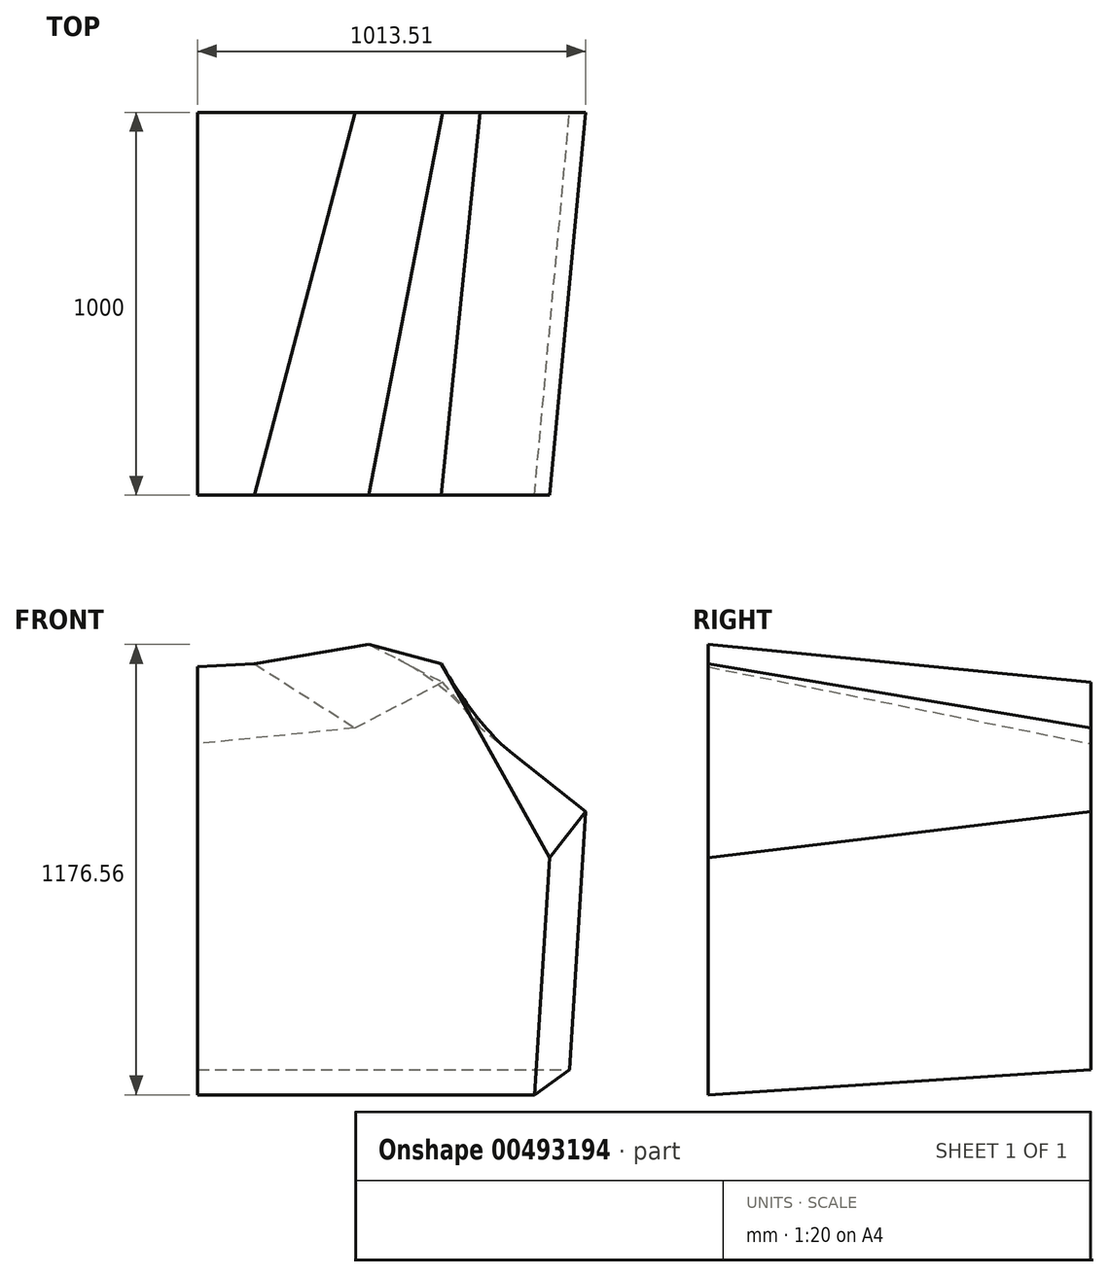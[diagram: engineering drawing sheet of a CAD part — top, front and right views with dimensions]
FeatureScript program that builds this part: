
annotation { "Feature Type Name" : "Feature", "Feature Type Description" : "" }
export const myFeature = defineFeature(function(context is Context, id is Id, definition is map)
    precondition{}
    {
        {
            var Q0;
            Q0=qCreatedBy(makeId("Front.planeOp"),FACE);
            var sketch = newSketch(context, id + "F0", { "sketchPlane" : qUnion([Q0])});
            skLineSegment(sketch, "E0", {"start": v(0, 0) * mm, "end": v(0, 850.8) * mm});
            skLineSegment(sketch, "E1", {"start": v(0, 0) * mm, "end": v(971.51, 0) * mm});
            skLineSegment(sketch, "E2", {"start": v(971.51, 0) * mm, "end": v(1004.74, 533.03) * mm});
            skLineSegment(sketch, "E3", {"start": v(1004.74, 533.03) * mm, "end": v(971.51, 0) * mm});
            skLineSegment(sketch, "E4", {"start": v(971.51, 0) * mm, "end": v(1013.5, 673.7) * mm});
            skLineSegment(sketch, "E5", {"start": v(1013.5, 673.7) * mm, "end": v(737.82, 892.07) * mm});
            skLineSegment(sketch, "E6", {"start": v(737.82, 892.07) * mm, "end": v(640.53, 1011.26) * mm});
            skLineSegment(sketch, "E7", {"start": v(640.53, 1011.26) * mm, "end": v(411.88, 892.07) * mm});
            skLineSegment(sketch, "E8", {"start": v(411.88, 892.07) * mm, "end": v(0, 850.8) * mm});
            skLineSegment(sketch, "E9", {"start": v(0, 850.8) * mm, "end": v(0, 850.8) * mm});
            skSolve(sketch);
        }
        {
            var Q0;
            Q0=makeQuery(id+"F0.imprint","IMPRINT",FACE,{"disambiguationData":[TD([[makeQuery(id+"F0.imprint","IMPRINT",EDGE,{"derivedFrom":sQuery(id+"F0.wireOp",EDGE,"E0")}),-1.0]])]});
            cPlane(context, id + "F1", {"entities" : qUnion([Q0]), "cplaneType" : CPlaneType.OFFSET, "offset" : 1000 * mm, "width" : 152.4 * mm, "height" : 152.4 * mm});
        }
        {
            var Q0;
            Q0=qCreatedBy(id+"F1.planeOp",FACE);
            var sketch = newSketch(context, id + "F2", { "sketchPlane" : qUnion([Q0])});
            skLineSegment(sketch, "E10", {"start": v(0, -66.19) * mm, "end": v(0, 1051.66) * mm});
            skLineSegment(sketch, "E11", {"start": v(0, -66.19) * mm, "end": v(879.93, -66.19) * mm});
            skLineSegment(sketch, "E12", {"start": v(879.93, -66.19) * mm, "end": v(913.65, 466.81) * mm});
            skLineSegment(sketch, "E13", {"start": v(913.65, 466.81) * mm, "end": v(879.93, -66.19) * mm});
            skLineSegment(sketch, "E14", {"start": v(879.93, -66.19) * mm, "end": v(919.13, 553.43) * mm});
            skLineSegment(sketch, "E15", {"start": v(919.13, 553.43) * mm, "end": v(636.53, 1059.64) * mm});
            skLineSegment(sketch, "E16", {"start": v(447.44, 1110.37) * mm, "end": v(636.53, 1059.64) * mm});
            skLineSegment(sketch, "E17", {"start": v(447.44, 1110.37) * mm, "end": v(148.94, 1059.64) * mm});
            skLineSegment(sketch, "E18", {"start": v(0, 1051.66) * mm, "end": v(148.94, 1059.64) * mm});
            skLineSegment(sketch, "E19", {"start": v(0, 1051.66) * mm, "end": v(0, 1051.66) * mm});
            skSolve(sketch);
        }
        {
            var Q0;
            Q0=makeQuery(id+"F2.imprint","IMPRINT",FACE,{"disambiguationData":[TD([[makeQuery(id+"F2.imprint","IMPRINT",EDGE,{"derivedFrom":sQuery(id+"F2.wireOp",EDGE,"E10")}),-1.0]])]});
            var Q1;
            Q1=makeQuery(id+"F0.imprint","IMPRINT",FACE,{"disambiguationData":[TD([[makeQuery(id+"F0.imprint","IMPRINT",EDGE,{"derivedFrom":sQuery(id+"F0.wireOp",EDGE,"E0")}),-1.0]])]});
            loft(context, id + "F3", {"sheetProfilesArray" : [{ "sheetProfileEntities" : qUnion([Q0]) }, { "sheetProfileEntities" : qUnion([Q1]) }]});
        }
    });
